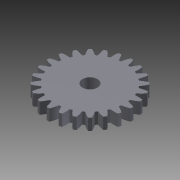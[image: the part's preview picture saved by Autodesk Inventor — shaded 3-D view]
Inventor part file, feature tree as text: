
AUTODESK INVENTOR PART (.ipt)
format: ipt  version: 2014 (Build 180170000, 170)  size: 220,160 bytes
history: native  units: mm (DEFAULTED — no unit token found)
features: plane x3, other x3, sketch x3, extrude x2
ambient origin geometry x8: Origin, YZ Plane, XZ Plane, XY Plane, X Axis, Y Axis, Z Axis, Center Point
bodies: Solid1 (feature_tree)
feature tree (11):
  extrude  "Extrusion1"  Depth=4.0mm TaperAngle=0.0deg
  plane  "Work Plane2"
  plane  "Work Plane8"
  plane  "Work Plane9"
  other  "平歯車"
  extrude  "押し出し2"  Depth=10.0mm TaperAngle=0.0deg
  sketch  "Sketch1"  dims[d0=29.222366mm d1=4.0mm d2=0.0mm]
  sketch  "Sketch2"  dims[d3=27.272727mm d4=10.0mm d5=0.0mm d16=37.5mm d17=0.0mm d34=1.308997mm d39=0.0mm d41=0.0mm d43=37.5mm d46=37.5mm d47=0.0mm d48=0.0mm d49=5.2mm d50=10.0mm d51=0.0mm]
  other  "Srf1"
  sketch  "スケッチ3"
  other  "ピッチ円直径"
